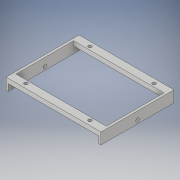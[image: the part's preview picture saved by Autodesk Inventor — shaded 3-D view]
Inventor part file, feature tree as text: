
AUTODESK INVENTOR PART (.ipt)
format: ipt  version: 2019 (Build 230136000, 136)  size: 143,872 bytes
history: native  units: in
note: dims shown in document units (in); Inventor stores cm internally (conversion verified against a paired STEP export)
features: sketch x4, extrude x2, hole x2
ambient origin geometry x8: Origin, YZ Plane, XZ Plane, XY Plane, X Axis, Y Axis, Z Axis, Center Point
bodies: Solid1 (feature_tree)
feature tree (8):
  extrude  "Extrusion1"  Depth=3.2283in
  extrude  "Extrusion2"  Depth=2.55in
  sketch  "Sketch3"  dims[d4=0.2in d5=0.0in d6=0.3in d7=0.0in]
  hole  "Hole2"  [1 undecoded]
  hole  "Hole3"  [1 undecoded]
  sketch  "Sketch1"  dims[d0=4.2in d1=3.2283in]
  sketch  "Sketch2"  dims[d2=4.0in d3=2.55in]
  sketch  "Sketch4"  dims[d8=2.8346in d9=2.8346in d20=0.15in d21=0.625in d22=0.375in d23=0.25in d24=0.5635in d25=1.0in d26=0.8108in d27=0.15in d28=0.625in d29=0.279in d30=0.25in d31=0.5635in d32=1.0in d33=0.8108in d13=1.0in d14=1.0in d15=1.0in d16=0.15in d17=0.25in d18=0.375in d19=0.5635in]
note: 2 required parameter values undecoded (feature->parameter linkage not recoverable at this tier; creation-order binding heuristic only, values carry confidence <= 0.55)
